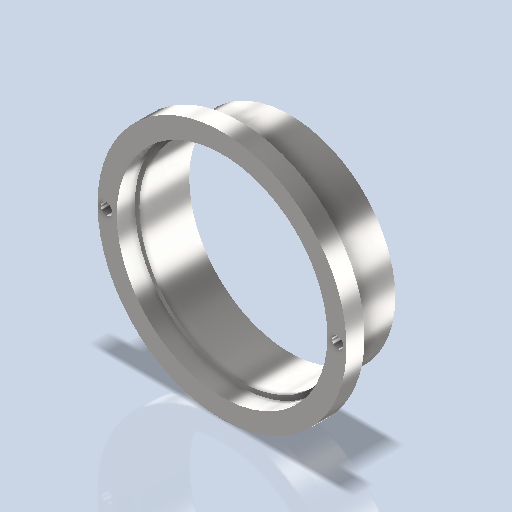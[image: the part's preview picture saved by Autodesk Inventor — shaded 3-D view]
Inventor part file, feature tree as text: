
AUTODESK INVENTOR PART (.ipt)
format: ipt  version: 2024.2 (Build 282272000, 272)  size: 281,600 bytes
history: native  units: mm
features: sketch x2, extrude x2, hole x1
ambient origin geometry x8: Origin, YZ Plane, XZ Plane, XY Plane, X Axis, Y Axis, Z Axis, Center Point
bodies: Volumenkörper1 (feature_tree)
feature tree (5):
  sketch  "Skizze1"  dims[d0=275.0mm d1=232.5mm]
  extrude  "Extrusion1"  Depth=232.5mm
  extrude  "Extrusion2"  Depth=20.0mm TaperAngle=0.0deg
  hole  "Bohrung1"  [1 undecoded]
  sketch  "Skizze2"  dims[d2=222.5mm d3=20.0mm d4=0.0mm d5=55.0mm d6=0.0mm d7=12.5mm d8=6.0mm d9=4.0mm d10=2.0mm d11=90.0deg d12=20.0mm d13=0.0mm d14=127.5mm d15=127.5mm]
note: 1 required parameter value undecoded (feature->parameter linkage not recoverable at this tier; creation-order binding heuristic only, values carry confidence <= 0.55)
